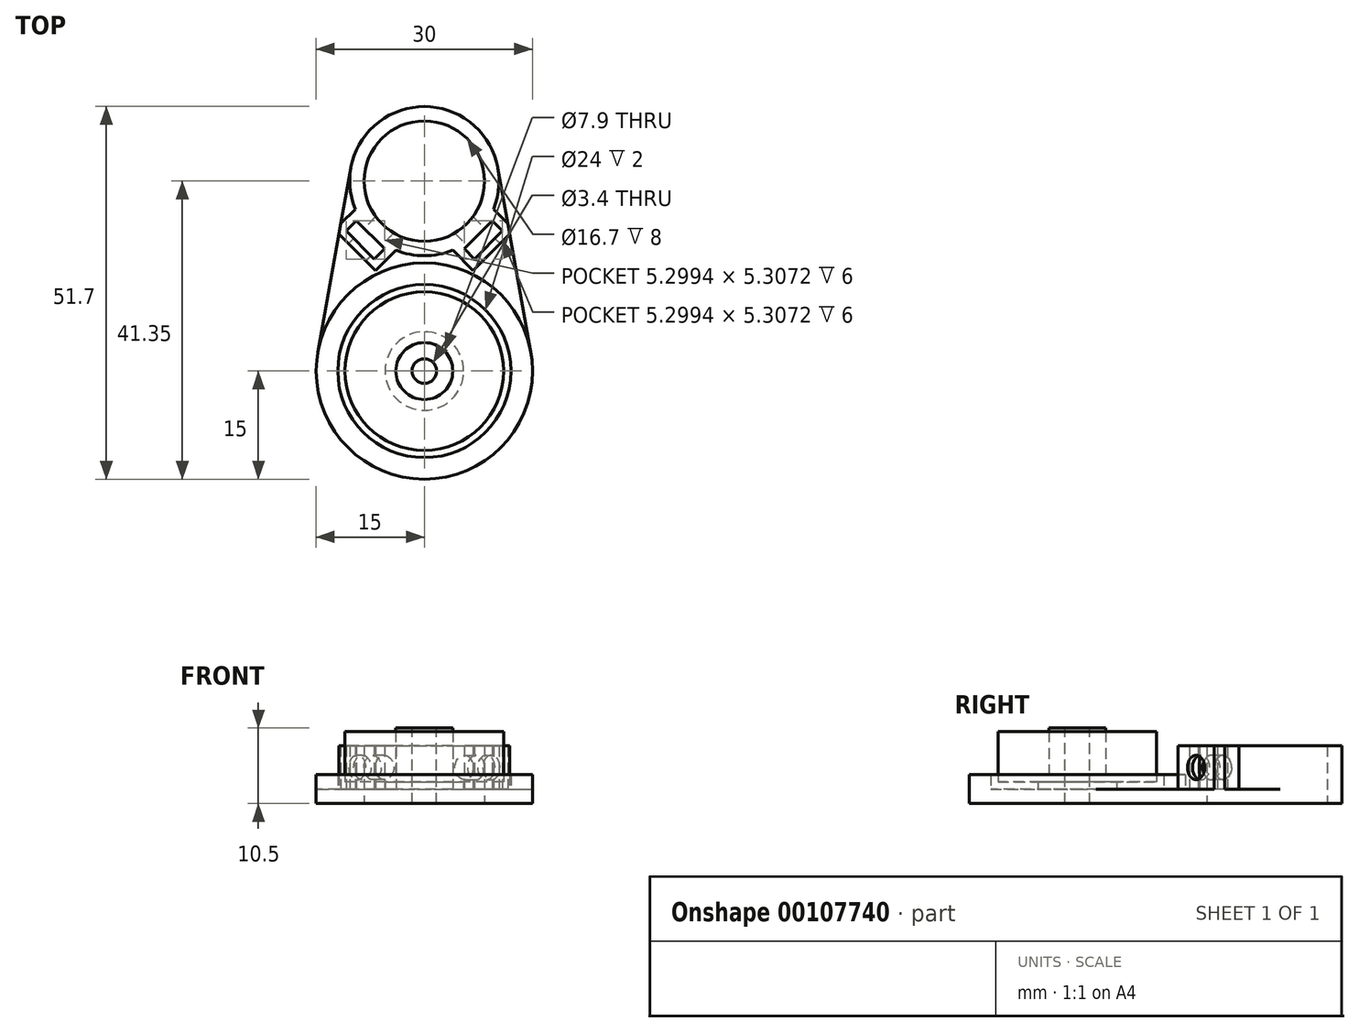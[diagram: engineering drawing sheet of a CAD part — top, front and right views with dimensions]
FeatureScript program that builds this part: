
annotation { "Feature Type Name" : "Feature", "Feature Type Description" : "" }
export const myFeature = defineFeature(function(context is Context, id is Id, definition is map)
    precondition{}
    {
        {
            assignVariable(context, id + "F0", {"name" : "BearingHeight", "anyValue" : 7});
        }
        {
            var Q0;
            Q0=qCreatedBy(makeId("Front.planeOp"),FACE);
            var sketch = newSketch(context, id + "F1", { "sketchPlane" : qUnion([Q0])});
            skLineSegment(sketch, "E0", {"start": v(0, 0) * mm, "end": v(0, 10.5) * mm});
            skLineSegment(sketch, "E1", {"start": v(0, 10.5) * mm, "end": v(3.95, 10.5) * mm});
            skLineSegment(sketch, "E2", {"start": v(3.95, 10.5) * mm, "end": v(3.95, 3) * mm});
            skLineSegment(sketch, "E3", {"start": v(3.95, 3) * mm, "end": v(5.45, 3) * mm});
            skLineSegment(sketch, "E4", {"start": v(5.45, 3) * mm, "end": v(5.45, 2) * mm});
            skLineSegment(sketch, "E5", {"start": v(5.45, 2) * mm, "end": v(11, 2) * mm});
            skLineSegment(sketch, "E6", {"start": v(11, 2) * mm, "end": v(12, 2) * mm});
            skLineSegment(sketch, "E7", {"start": v(12, 2) * mm, "end": v(12, 4) * mm});
            skLineSegment(sketch, "E8", {"start": v(12, 4) * mm, "end": v(15, 4) * mm});
            skLineSegment(sketch, "E9", {"start": v(15, 4) * mm, "end": v(15, 0) * mm});
            skLineSegment(sketch, "E10", {"start": v(15, 0) * mm, "end": v(0, 0) * mm});
            skSolve(sketch);
        }
        {
            var Q0;
            Q0=qSketchRegion(id+"F1",true);
            var Q1;
            Q1=sQuery(id+"F1.wireOp",EDGE,"E0");
            revolve(context, id + "F2", {"entities" : qUnion([Q0]), "axis" : qUnion([Q1]), "revolveType" : RevolveType.FULL});
        }
        {
            var Q0;
            Q0=makeQuery(id+"F2.opRevolve","SWEPT_FACE",FACE,{"disambiguationData":[OSD([sQuery(id+"F1.wireOp",EDGE,"E1")])]});
            var sketch = newSketch(context, id + "F3", { "sketchPlane" : qUnion([Q0])});
            skCircle(sketch, "E11", {"center": v(0, 0) * mm, "radius": 1.7 * mm});
            skSolve(sketch);
        }
        {
            var Q0;
            Q0=makeQuery(id+"F3.imprint","IMPRINT",FACE,{"disambiguationData":[TD([[makeQuery(id+"F3.imprint","IMPRINT",EDGE,{"derivedFrom":sQuery(id+"F3.wireOp",EDGE,"E11")}),1.0]])]});
            extrude(context, id + "F4", {"entities" : qUnion([Q0]), "operationType" : NewBodyOperationType.REMOVE, "endBound" : BoundingType.UP_TO_NEXT, "oppositeDirection" : true, "depth" : 25 * mm});
        }
        {
            var Q0;
            Q0=makeQuery(id+"F2.opRevolve","SWEPT_FACE",FACE,{"disambiguationData":[OSD([sQuery(id+"F1.wireOp",EDGE,"E10")])]});
            var sketch = newSketch(context, id + "F5", { "sketchPlane" : qUnion([Q0])});
            skCircle(sketch, "E12.0", {"center": v(0, 0) * mm, "radius": 15 * mm});
            skLineSegment(sketch, "E13", {"start": v(0, -26.35) * mm, "end": v(0, 0) * mm, "construction": true});
            skCircle(sketch, "E14", {"center": v(0, -26.35) * mm, "radius": 10.35 * mm});
            skLineSegment(sketch, "E15", {"start": v(-14.76, -2.65) * mm, "end": v(-10.19, -28.18) * mm});
            skLineSegment(sketch, "E16", {"start": v(14.76, -2.65) * mm, "end": v(10.19, -28.18) * mm});
            skCircle(sketch, "E17", {"center": v(0, -26.35) * mm, "radius": 8.35 * mm});
            skLineSegment(sketch, "E18", {"start": v(-3.94, -16.78) * mm, "end": v(-6.77, -13.95) * mm});
            skLineSegment(sketch, "E19", {"start": v(-6.77, -13.95) * mm, "end": v(-12.42, -19.62) * mm});
            skLineSegment(sketch, "E20", {"start": v(-12.42, -19.62) * mm, "end": v(-9.58, -22.44) * mm});
            skLineSegment(sketch, "E21", {"start": v(0, -26.35) * mm, "end": v(-9.6, -16.79) * mm, "construction": true});
            skLineSegment(sketch, "E22.bottom", {"start": v(-9.41, -20.85) * mm, "end": v(-5.53, -16.96) * mm});
            skLineSegment(sketch, "E22.top", {"start": v(-10.83, -19.44) * mm, "end": v(-6.94, -15.55) * mm});
            skLineSegment(sketch, "E22.left", {"start": v(-9.41, -20.85) * mm, "end": v(-10.83, -19.44) * mm});
            skLineSegment(sketch, "E22.right", {"start": v(-5.53, -16.96) * mm, "end": v(-6.94, -15.55) * mm});
            skPoint(sketch, "E22.middle", {"position": v(-8.18, -18.2) * mm});
            skLineSegment(sketch, "E23.MirrorCS", {"start": v(5.53, -16.96) * mm, "end": v(6.94, -15.55) * mm});
            skLineSegment(sketch, "E24.MirrorCS", {"start": v(3.94, -16.78) * mm, "end": v(6.77, -13.95) * mm});
            skPoint(sketch, "E25.MirrorP", {"position": v(8.18, -18.2) * mm});
            skLineSegment(sketch, "E26.MirrorCS", {"start": v(12.42, -19.62) * mm, "end": v(9.58, -22.44) * mm});
            skLineSegment(sketch, "E27.MirrorCS", {"start": v(9.41, -20.85) * mm, "end": v(10.83, -19.44) * mm});
            skLineSegment(sketch, "E28.MirrorCS", {"start": v(10.83, -19.44) * mm, "end": v(6.94, -15.55) * mm});
            skLineSegment(sketch, "E29.MirrorCS", {"start": v(6.77, -13.95) * mm, "end": v(12.42, -19.62) * mm});
            skLineSegment(sketch, "E30.MirrorCS", {"start": v(9.41, -20.85) * mm, "end": v(5.53, -16.96) * mm});
            skSolve(sketch);
        }
        {
            var Q0;
            {var subQ0=sQuery(id+"F5.wireOp",EDGE,"E16");Q0=makeQuery(id+"F5.imprint","IMPRINT",FACE,{"disambiguationData":[TD([[makeQuery(id+"F5.imprint","IMPRINT",EDGE,{"derivedFrom":subQ0}),-1.0]])]});}
            var Q1;
            Q1=makeQuery(id+"F5.imprint","IMPRINT",FACE,{"disambiguationData":[TD([[makeQuery(id+"F5.imprint","IMPRINT",EDGE,{"derivedFrom":sQuery(id+"F5.wireOp",EDGE,"E17")}),-1.0]])]});
            var Q2;
            {var subQ0=sQuery(id+"F5.wireOp",EDGE,"E18");Q2=makeQuery(id+"F5.imprint","IMPRINT",FACE,{"disambiguationData":[TD([[makeQuery(id+"F5.imprint","IMPRINT",EDGE,{"derivedFrom":subQ0}),1.0]])]});}
            var Q3;
            {var subQ1=sQuery(id+"F5.wireOp",EDGE,"E22.bottom");Q3=makeQuery(id+"F5.imprint","IMPRINT",FACE,{"disambiguationData":[TD([[makeQuery(id+"F5.imprint","IMPRINT",EDGE,{"derivedFrom":subQ1}),1.0]])]});}
            var Q4;
            {var subQ0=sQuery(id+"F5.wireOp",EDGE,"E15");var subQ1=sQuery(id+"F5.wireOp",EDGE,"E14");var subQ2=makeQuery(id+"F5.imprint","INTERSECT",VERTEX,{"derivedFrom":[subQ1,subQ0]});Q4=makeQuery(id+"F5.imprint","IMPRINT",FACE,{"disambiguationData":[TD([[makeQuery(id+"F5.imprint","IMPRINT",EDGE,{"disambiguationData":[TD([[subQ2,1.0]])],"derivedFrom":subQ1}),-1.0]])]});}
            var Q5;
            Q5=makeQuery(id+"F5.imprint","IMPRINT",FACE,{"disambiguationData":[TD([[makeQuery(id+"F5.imprint","IMPRINT",EDGE,{"derivedFrom":makeQuery(id+"F4.boolean.opBoolean","COPY",EDGE,{"derivedFrom":makeQuery(id+"F4.opExtrude","TWEAK_EDGE",EDGE,{"derivedFrom":[makeQuery(id+"F2.opRevolve","SWEPT_FACE",FACE,{"disambiguationData":[OSD([sQuery(id+"F1.wireOp",EDGE,"E10")])]}),makeQuery(id+"F3.imprint","IMPRINT",EDGE,{"derivedFrom":sQuery(id+"F3.wireOp",EDGE,"E11")})]})})}),-1.0]])]});
            var Q6;
            Q6=makeQuery(id+"F2.opRevolve","SWEPT_FACE",FACE,{"disambiguationData":[OSD([sQuery(id+"F1.wireOp",EDGE,"E10")])]});
            var Q7;
            Q7=makeQuery(id+"F5.imprint","IMPRINT",FACE,{"disambiguationData":[TD([[makeQuery(id+"F5.imprint","IMPRINT",EDGE,{"derivedFrom":sQuery(id+"F5.wireOp",EDGE,"E23.MirrorCS")}),1.0]])]});
            var Q8;
            Q8=makeQuery(id+"F5.imprint","IMPRINT",FACE,{"disambiguationData":[TD([[makeQuery(id+"F5.imprint","IMPRINT",EDGE,{"derivedFrom":sQuery(id+"F5.wireOp",EDGE,"E23.MirrorCS")}),-1.0]])]});
            var Q9;
            {var subQ10=sQuery(id+"F5.wireOp",EDGE,"E18");Q9=makeQuery(id+"F5.imprint","IMPRINT",FACE,{"disambiguationData":[TD([[makeQuery(id+"F5.imprint","IMPRINT",EDGE,{"derivedFrom":subQ10}),-1.0]])]});}
            var Q10;
            Q10=makeQuery(id+"F2.opRevolve","SWEPT_FACE",FACE,{"disambiguationData":[OSD([sQuery(id+"F1.wireOp",EDGE,"E5"),sQuery(id+"F1.wireOp",EDGE,"E6")])]});
            extrude(context, id + "F6", {"entities" : qUnion([Q0, Q1, Q2, Q3, Q4, Q5, Q6, Q7, Q8, Q9]), "operationType" : NewBodyOperationType.ADD, "endBound" : BoundingType.UP_TO_SURFACE, "oppositeDirection" : true, "endBoundEntityFace" : qUnion([Q10]), "depth" : 25 * mm});
        }
        {
            var Q0;
            Q0=makeQuery(id+"F5.imprint","IMPRINT",FACE,{"disambiguationData":[TD([[makeQuery(id+"F5.imprint","IMPRINT",EDGE,{"derivedFrom":sQuery(id+"F5.wireOp",EDGE,"E17")}),-1.0]])]});
            var Q1;
            {var subQ0=sQuery(id+"F5.wireOp",EDGE,"E18");Q1=makeQuery(id+"F5.imprint","IMPRINT",FACE,{"disambiguationData":[TD([[makeQuery(id+"F5.imprint","IMPRINT",EDGE,{"derivedFrom":subQ0}),1.0]])]});}
            var Q2;
            Q2=makeQuery(id+"F5.imprint","IMPRINT",FACE,{"disambiguationData":[TD([[makeQuery(id+"F5.imprint","IMPRINT",EDGE,{"derivedFrom":sQuery(id+"F5.wireOp",EDGE,"E23.MirrorCS")}),1.0]])]});
            extrude(context, id + "F7", {"entities" : qUnion([Q0, Q1, Q2]), "operationType" : NewBodyOperationType.ADD, "oppositeDirection" : true, "depth" : 8 * mm});
        }
        {
            var Q0;
            Q0=makeQuery(id+"F7.opExtrude","SWEPT_FACE",FACE,{"disambiguationData":[OSD([sQuery(id+"F5.wireOp",EDGE,"E19")])]});
            var sketch = newSketch(context, id + "F8", { "sketchPlane" : qUnion([Q0])});
            skLineSegment(sketch, "E31", {"start": v(-14.66, 5) * mm, "end": v(-21.83, 5) * mm, "construction": true});
            skPoint(sketch, "E32", {"position": v(-18.24, 5) * mm});
            skCircle(sketch, "E33", {"center": v(-18.24, 5) * mm, "radius": 1.7 * mm});
            skSolve(sketch);
        }
        {
            var Q0;
            Q0=makeQuery(id+"F8.imprint","IMPRINT",FACE,{"disambiguationData":[TD([[makeQuery(id+"F8.imprint","IMPRINT",EDGE,{"derivedFrom":sQuery(id+"F8.wireOp",EDGE,"E33")}),1.0]])]});
            var Q1;
            {var subQ0=sQuery(id+"F5.wireOp",EDGE,"E17");Q1=makeQuery(id+"F7.boolean.opBoolean","MERGE",FACE,{"derivedFrom":[makeQuery(id+"F6.opExtrude","SWEPT_FACE",FACE,{"disambiguationData":[OSD([subQ0])]}),makeQuery(id+"F7.opExtrude","SWEPT_FACE",FACE,{"disambiguationData":[OSD([subQ0])]})]});}
            extrude(context, id + "F9", {"entities" : qUnion([Q0]), "operationType" : NewBodyOperationType.REMOVE, "endBound" : BoundingType.UP_TO_SURFACE, "oppositeDirection" : true, "endBoundEntityFace" : qUnion([Q1]), "depth" : 25 * mm});
        }
        {
            var Q0;
            Q0=makeQuery(id+"F7.opExtrude","SWEPT_FACE",FACE,{"disambiguationData":[OSD([sQuery(id+"F5.wireOp",EDGE,"E29.MirrorCS")])]});
            var sketch = newSketch(context, id + "F10", { "sketchPlane" : qUnion([Q0])});
            skLineSegment(sketch, "E34", {"start": v(18.24, 2) * mm, "end": v(18.24, 8) * mm, "construction": true});
            skPoint(sketch, "E35", {"position": v(18.24, 5) * mm});
            skCircle(sketch, "E36", {"center": v(18.24, 5) * mm, "radius": 1.7 * mm});
            skSolve(sketch);
        }
        {
            var Q0;
            Q0=makeQuery(id+"F10.imprint","IMPRINT",FACE,{"disambiguationData":[TD([[makeQuery(id+"F10.imprint","IMPRINT",EDGE,{"derivedFrom":sQuery(id+"F10.wireOp",EDGE,"E36")}),1.0]])]});
            var Q1;
            {var subQ0=sQuery(id+"F5.wireOp",EDGE,"E17");Q1=makeQuery(id+"F7.boolean.opBoolean","MERGE",FACE,{"derivedFrom":[makeQuery(id+"F6.opExtrude","SWEPT_FACE",FACE,{"disambiguationData":[OSD([subQ0])]}),makeQuery(id+"F7.opExtrude","SWEPT_FACE",FACE,{"disambiguationData":[OSD([subQ0])]})]});}
            extrude(context, id + "F11", {"entities" : qUnion([Q0]), "operationType" : NewBodyOperationType.REMOVE, "endBound" : BoundingType.UP_TO_SURFACE, "oppositeDirection" : true, "endBoundEntityFace" : qUnion([Q1]), "depth" : 25 * mm});
        }
        {
            var Q0;
            Q0=makeQuery(id+"F2.opRevolve","SWEPT_FACE",FACE,{"disambiguationData":[OSD([sQuery(id+"F1.wireOp",EDGE,"E3")])]});
            var sketch = newSketch(context, id + "F12", { "sketchPlane" : qUnion([Q0])});
            skCircle(sketch, "E37.0", {"center": v(0, 0) * mm, "radius": 3.95 * mm});
            skCircle(sketch, "E38", {"center": v(0, 0) * mm, "radius": 11 * mm});
            skSolve(sketch);
        }
        {
            var Q0;
            Q0=qSketchRegion(id+"F12",true);
            extrude(context, id + "F13", {"entities" : qUnion([Q0]), "depth" : (getVariable(context, 'BearingHeight')) * mm});
        }
    });
